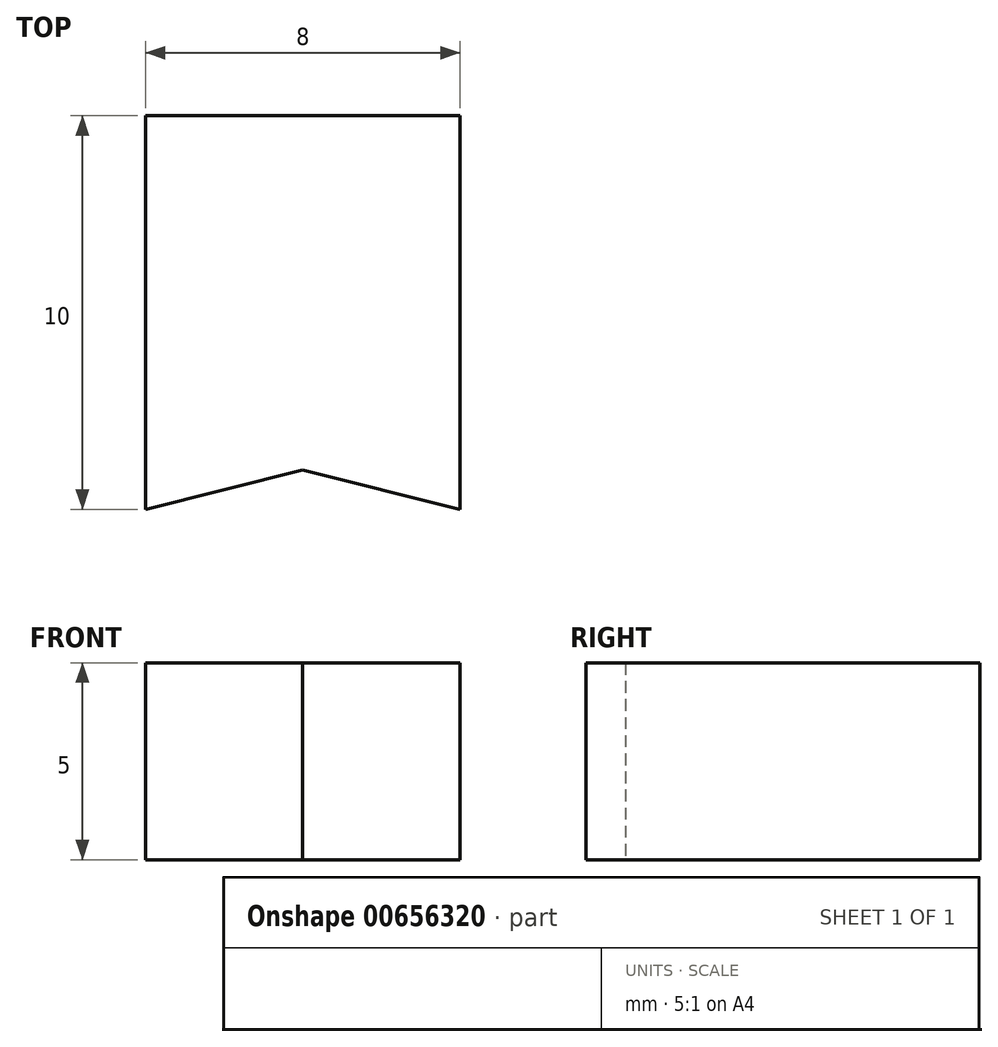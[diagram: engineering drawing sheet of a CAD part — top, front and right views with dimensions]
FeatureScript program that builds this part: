
annotation { "Feature Type Name" : "Feature", "Feature Type Description" : "" }
export const myFeature = defineFeature(function(context is Context, id is Id, definition is map)
    precondition{}
    {
        {
            var Q0;
            Q0=qCreatedBy(makeId("Top.planeOp"),FACE);
            var sketch = newSketch(context, id + "F0", { "sketchPlane" : qUnion([Q0])});
            skLineSegment(sketch, "E0.bottom", {"start": v(-4, -10) * mm, "end": v(4, -10) * mm, "construction": true});
            skLineSegment(sketch, "E0.top", {"start": v(-4, 0) * mm, "end": v(4, 0) * mm});
            skLineSegment(sketch, "E0.left", {"start": v(-4, -10) * mm, "end": v(-4, 0) * mm});
            skLineSegment(sketch, "E0.right", {"start": v(4, -10) * mm, "end": v(4, 0) * mm});
            skPoint(sketch, "E1", {"position": v(0, 0) * mm});
            skLineSegment(sketch, "E2", {"start": v(0, -10) * mm, "end": v(0, -9) * mm, "construction": true});
            skLineSegment(sketch, "E3", {"start": v(-4, -10) * mm, "end": v(0, -9) * mm});
            skLineSegment(sketch, "E4", {"start": v(4, -10) * mm, "end": v(0, -9) * mm});
            skSolve(sketch);
        }
        {
            var Q0;
            Q0 = qSketchRegion(id + "F0", true);
            extrude(context, id + "F1", {"entities" : qUnion([Q0]), "depth" : 5 * mm, "offsetDistance" : 25 * mm});
        }
    });
